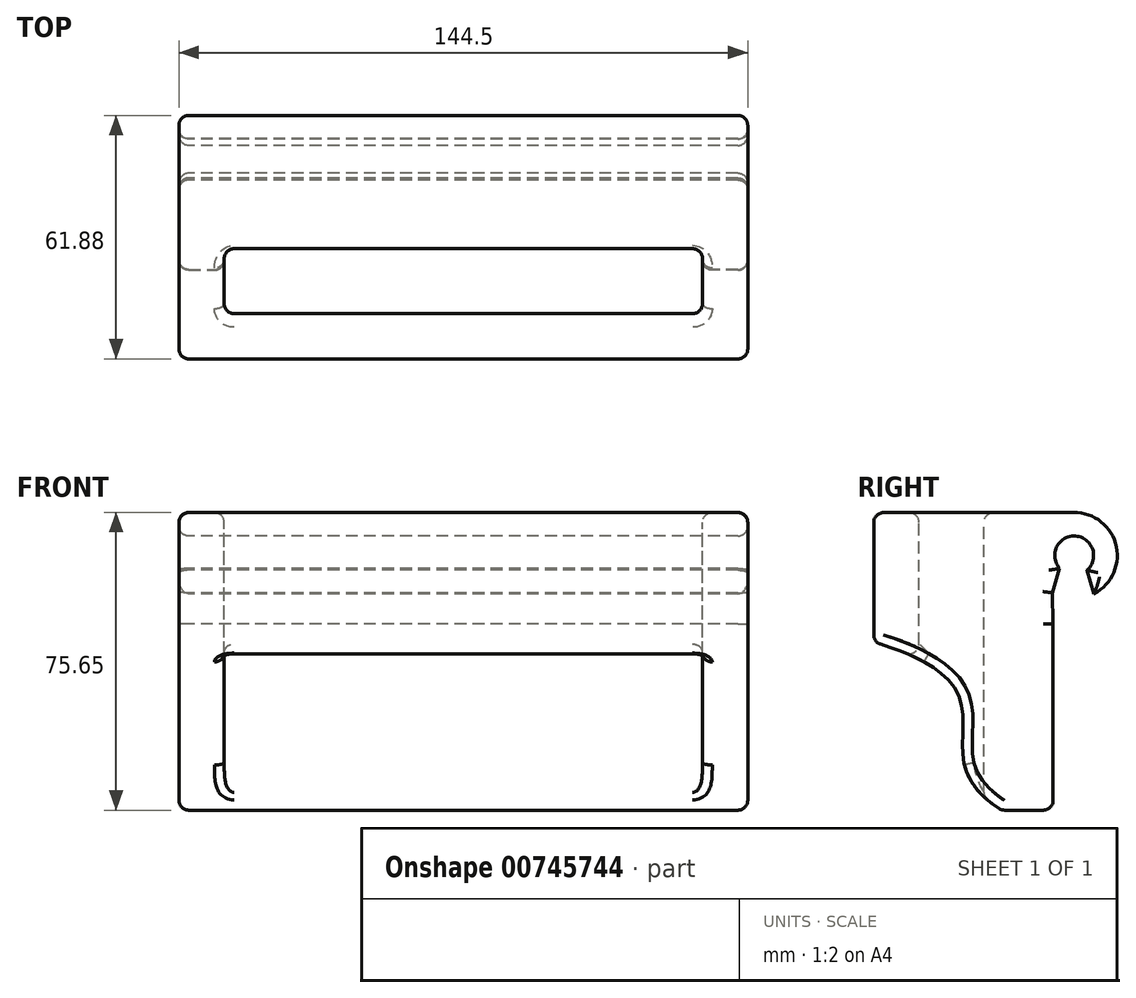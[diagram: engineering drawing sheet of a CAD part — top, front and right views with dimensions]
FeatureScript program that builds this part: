
annotation { "Feature Type Name" : "Feature", "Feature Type Description" : "" }
export const myFeature = defineFeature(function(context is Context, id is Id, definition is map)
    precondition{}
    {
        {
            var Q0;
            Q0=qCreatedBy(makeId("Right.planeOp"),FACE);
            var sketch = newSketch(context, id + "F0", { "sketchPlane" : qUnion([Q0])});
            skLineSegment(sketch, "E0", {"start": v(51.34, -49.28) * mm, "end": v(51.34, -37.74) * mm});
            skLineSegment(sketch, "E1", {"start": v(51.34, -49.28) * mm, "end": v(51.34, -85.02) * mm});
            skLineSegment(sketch, "E2", {"start": v(51.34, -85.02) * mm, "end": v(38.18, -85.02) * mm});
            skFitSpline(sketch, "E3", {"points": [v(5.66, -42.27) * mm, v(38.18, -85.02) * mm], "startDerivative": vector(123.86, -37.24) * mm, "endDerivative": vector(71.5, -46.02) * mm});
            skCircle(sketch, "E4", {"center": v(56.7, -20.32) * mm, "radius": 4.95 * mm});
            skPoint(sketch, "E4.first.point", {"position": v(51.82, -19.44) * mm});
            skPoint(sketch, "E4.second.point", {"position": v(61.12, -18.1) * mm});
            skPoint(sketch, "E4.third.point", {"position": v(61.55, -19.35) * mm});
            skPoint(sketch, "E4.third.point.positionSnap0", {"position": v(51.34, -19.35) * mm});
            skCircle(sketch, "E5.0", {"center": v(56.7, -20.32) * mm, "radius": 10.95 * mm});
            skLineSegment(sketch, "E6", {"start": v(51.34, -37.74) * mm, "end": v(51.23, -29.8) * mm});
            skLineSegment(sketch, "E7", {"start": v(51.23, -29.8) * mm, "end": v(52.97, -23.58) * mm});
            skLineSegment(sketch, "E8", {"start": v(59.96, -24.04) * mm, "end": v(61.74, -30.04) * mm});
            skLineSegment(sketch, "E9", {"start": v(55.48, -9.44) * mm, "end": v(5.76, -9.44) * mm});
            skLineSegment(sketch, "E10", {"start": v(5.76, -9.44) * mm, "end": v(5.76, -42.3) * mm});
            skSolve(sketch);
        }
        {
            var Q0;
            Q0=makeQuery(id+"F0.imprint","IMPRINT",FACE,{"disambiguationData":[TD([[makeQuery(id+"F0.imprint","IMPRINT",EDGE,{"derivedFrom":sQuery(id+"F0.wireOp",EDGE,"E0")}),1.0]])]});
            var Q1;
            {var subQ3=sQuery(id+"F0.wireOp",EDGE,"E7");Q1=makeQuery(id+"F0.imprint","IMPRINT",FACE,{"disambiguationData":[TD([[makeQuery(id+"F0.imprint","IMPRINT",EDGE,{"derivedFrom":subQ3}),1.0]])]});}
            extrude(context, id + "F1", {"entities" : qUnion([Q0, Q1]), "depth" : 144.5 * mm, "offsetDistance" : 25 * mm});
        }
        {
            var Q0;
            Q0=makeQuery(id+"F1.opExtrude","SWEPT_FACE",FACE,{"disambiguationData":[OSD([sQuery(id+"F0.wireOp",EDGE,"E9")])]});
            var sketch = newSketch(context, id + "F2", { "sketchPlane" : qUnion([Q0])});
            skLineSegment(sketch, "E11.bottom", {"start": v(11.5, 33.76) * mm, "end": v(133, 33.76) * mm});
            skLineSegment(sketch, "E11.top", {"start": v(11.5, 17.26) * mm, "end": v(133, 17.26) * mm});
            skLineSegment(sketch, "E11.left", {"start": v(11.5, 33.76) * mm, "end": v(11.5, 17.26) * mm});
            skLineSegment(sketch, "E11.right", {"start": v(133, 33.76) * mm, "end": v(133, 17.26) * mm});
            skPoint(sketch, "E11.middle", {"position": v(72.25, 25.5) * mm});
            skPoint(sketch, "E11.middle.positionSnap0", {"position": v(4, 25.5) * mm});
            skSolve(sketch);
        }
        {
            var Q0;
            Q0=makeQuery(id+"F2.imprint","IMPRINT",FACE,{"disambiguationData":[TD([[makeQuery(id+"F2.imprint","IMPRINT",EDGE,{"derivedFrom":sQuery(id+"F2.wireOp",EDGE,"E11.bottom")}),-1.0]])]});
            extrude(context, id + "F3", {"entities" : qUnion([Q0]), "operationType" : NewBodyOperationType.REMOVE, "endBound" : BoundingType.THROUGH_ALL, "oppositeDirection" : true, "depth" : 25 * mm, "offsetDistance" : 25 * mm});
        }
        {
            var Q0;
            Q0=makeQuery(id+"F1.opExtrude","SWEPT_FACE",FACE,{"disambiguationData":[OSD([sQuery(id+"F0.wireOp",EDGE,"E10")])]});
            var Q1;
            Q1=makeQuery(id+"F1.opExtrude","SWEPT_FACE",FACE,{"disambiguationData":[OSD([sQuery(id+"F0.wireOp",EDGE,"E9")])]});
            var Q2;
            Q2=makeQuery(id+"F1.opExtrude","CAP_FACE",FACE,{"disambiguationData":[OSD([sQuery(id+"F0.wireOp",EDGE,"E0"),sQuery(id+"F0.wireOp",EDGE,"E1"),sQuery(id+"F0.wireOp",EDGE,"E2"),sQuery(id+"F0.wireOp",EDGE,"E3"),sQuery(id+"F0.wireOp",EDGE,"E4"),sQuery(id+"F0.wireOp",EDGE,"E5.0"),sQuery(id+"F0.wireOp",EDGE,"E6"),sQuery(id+"F0.wireOp",EDGE,"E7"),sQuery(id+"F0.wireOp",EDGE,"E8"),sQuery(id+"F0.wireOp",EDGE,"E9"),sQuery(id+"F0.wireOp",EDGE,"E10")])],"isStart":true});
            var Q3;
            Q3=makeQuery(id+"F1.opExtrude","SWEPT_FACE",FACE,{"disambiguationData":[OSD([sQuery(id+"F0.wireOp",EDGE,"E2")])]});
            var Q4;
            Q4=makeQuery(id+"F1.opExtrude","CAP_FACE",FACE,{"disambiguationData":[OSD([sQuery(id+"F0.wireOp",EDGE,"E0"),sQuery(id+"F0.wireOp",EDGE,"E1"),sQuery(id+"F0.wireOp",EDGE,"E2"),sQuery(id+"F0.wireOp",EDGE,"E3"),sQuery(id+"F0.wireOp",EDGE,"E4"),sQuery(id+"F0.wireOp",EDGE,"E5.0"),sQuery(id+"F0.wireOp",EDGE,"E6"),sQuery(id+"F0.wireOp",EDGE,"E7"),sQuery(id+"F0.wireOp",EDGE,"E8"),sQuery(id+"F0.wireOp",EDGE,"E9"),sQuery(id+"F0.wireOp",EDGE,"E10")])],"isStart":false});
            var Q5;
            Q5=makeQuery(id+"F1.opExtrude","SWEPT_FACE",FACE,{"disambiguationData":[OSD([sQuery(id+"F0.wireOp",EDGE,"E3")])]});
            var Q6;
            Q6=makeQuery(id+"F3.boolean.opBoolean","COPY",FACE,{"derivedFrom":makeQuery(id+"F3.opExtrude","SWEPT_FACE",FACE,{"disambiguationData":[OSD([sQuery(id+"F2.wireOp",EDGE,"E11.left")])]})});
            var Q7;
            Q7=makeQuery(id+"F3.boolean.opBoolean","COPY",FACE,{"derivedFrom":makeQuery(id+"F3.opExtrude","SWEPT_FACE",FACE,{"disambiguationData":[OSD([sQuery(id+"F2.wireOp",EDGE,"E11.right")])]})});
            fillet(context, id + "F4", {"entities" : qUnion([Q0, Q1, Q2, Q3, Q4, Q5, Q6, Q7]), "radius" : 2.5 * mm, "tangentPropagation" : true, "allowEdgeOverflow" : false});
        }
    });
